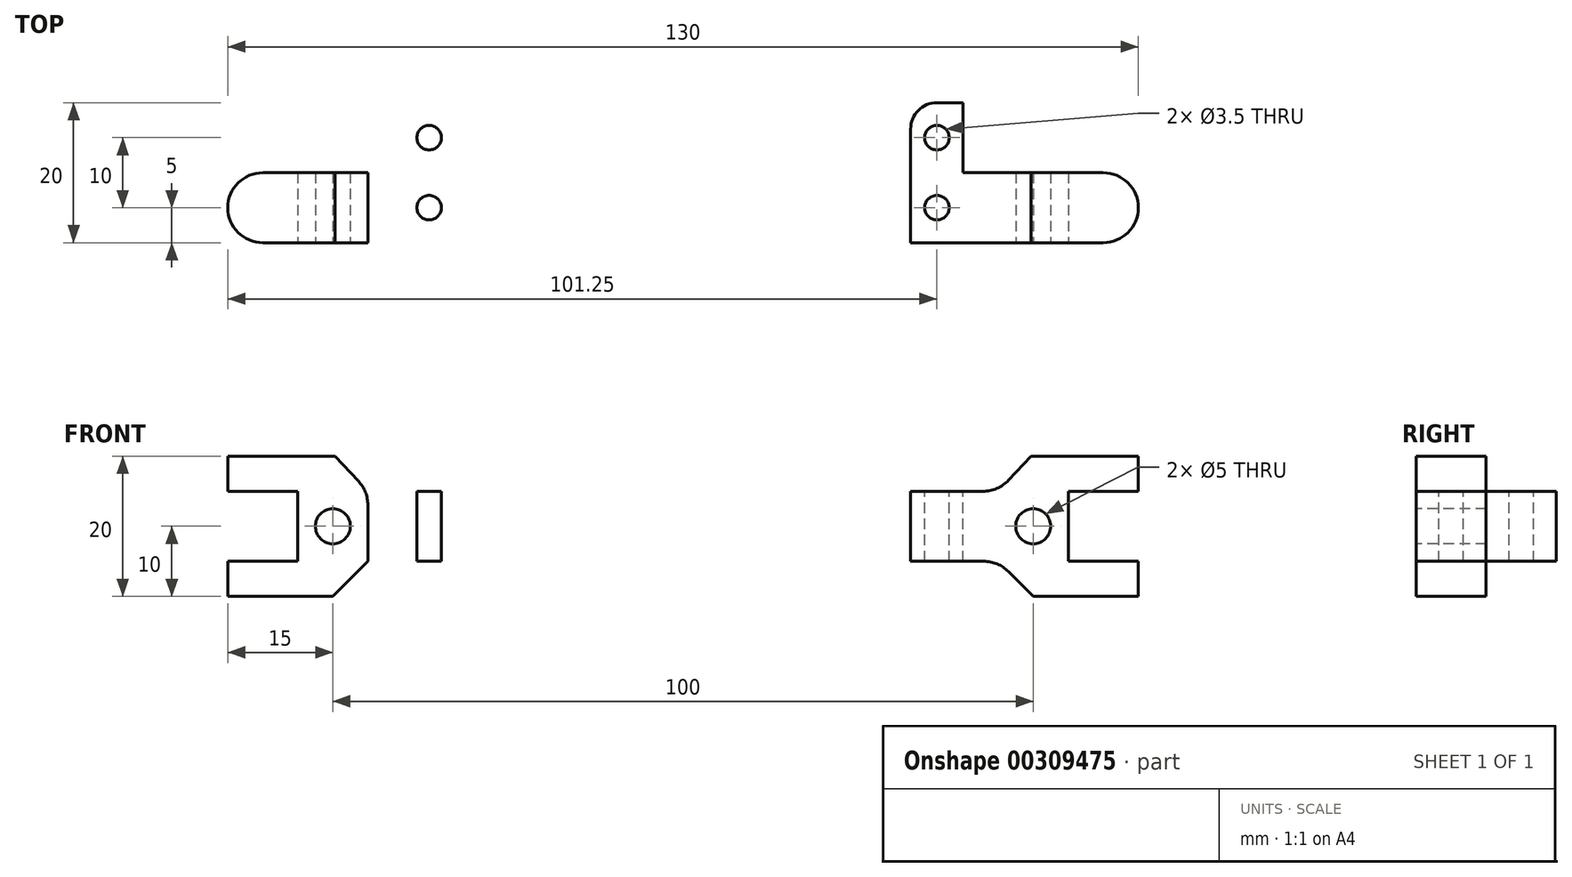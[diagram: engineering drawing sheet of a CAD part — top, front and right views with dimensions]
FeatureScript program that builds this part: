
annotation { "Feature Type Name" : "Feature", "Feature Type Description" : "" }
export const myFeature = defineFeature(function(context is Context, id is Id, definition is map)
    precondition{}
    {
        {
            var Q0;
            Q0=qCreatedBy(makeId("Top.planeOp"),FACE);
            var sketch = newSketch(context, id + "F0", { "sketchPlane" : qUnion([Q0])});
            skLineSegment(sketch, "E0.bottom", {"start": v(65, 5) * mm, "end": v(-65, 5) * mm});
            skLineSegment(sketch, "E0.top", {"start": v(65, -5) * mm, "end": v(-65, -5) * mm});
            skLineSegment(sketch, "E0.left", {"start": v(65, 5) * mm, "end": v(65, -5) * mm});
            skLineSegment(sketch, "E0.right", {"start": v(-65, 5) * mm, "end": v(-65, -5) * mm});
            skPoint(sketch, "E0.middle", {"position": v(0, 0) * mm});
            skSolve(sketch);
        }
        {
            var Q0;
            Q0 = qSketchRegion(id + "F0", true);
            extrude(context, id + "F1", {"entities" : qUnion([Q0]), "depth" : 20 * mm, "offsetDistance" : 25 * mm});
        }
        {
            var Q0;
            Q0=makeQuery(id+"F1.opExtrude","SWEPT_FACE",FACE,{"disambiguationData":[OSD([sQuery(id+"F0.wireOp",EDGE,"E0.top")])]});
            var sketch = newSketch(context, id + "F2", { "sketchPlane" : qUnion([Q0])});
            skLineSegment(sketch, "E1", {"start": v(0, 0) * mm, "end": v(0, 10) * mm});
            skLineSegment(sketch, "E2.bottom", {"start": v(-55, 15) * mm, "end": v(55, 15) * mm});
            skLineSegment(sketch, "E2.top", {"start": v(-55, 5) * mm, "end": v(55, 5) * mm});
            skLineSegment(sketch, "E2.left", {"start": v(-55, 15) * mm, "end": v(-55, 5) * mm});
            skLineSegment(sketch, "E2.right", {"start": v(55, 15) * mm, "end": v(55, 5) * mm});
            skPoint(sketch, "E2.middle", {"position": v(0, 10) * mm});
            skLineSegment(sketch, "E3", {"start": v(-55, 15) * mm, "end": v(-65, 15) * mm});
            skLineSegment(sketch, "E4", {"start": v(-55, 5) * mm, "end": v(-65, 5) * mm});
            skLineSegment(sketch, "E5", {"start": v(55, 15) * mm, "end": v(65, 15) * mm});
            skPoint(sketch, "E5.endSnap0", {"position": v(65, 10) * mm});
            skLineSegment(sketch, "E6", {"start": v(55, 5) * mm, "end": v(65, 5) * mm});
            skLineSegment(sketch, "E7", {"start": v(-55, 5) * mm, "end": v(-55, 0) * mm});
            skLineSegment(sketch, "E8", {"start": v(-55, 0) * mm, "end": v(-50, 0) * mm});
            skLineSegment(sketch, "E9", {"start": v(-50, 0) * mm, "end": v(-45, 5) * mm});
            skLineSegment(sketch, "E10", {"start": v(-54.7, 20) * mm, "end": v(-49.7, 20) * mm});
            skLineSegment(sketch, "E11", {"start": v(-45, 5) * mm, "end": v(-45, 15) * mm});
            skLineSegment(sketch, "E12", {"start": v(-45, 15) * mm, "end": v(-49.7, 20) * mm});
            skLineSegment(sketch, "E13", {"start": v(-45, 15) * mm, "end": v(-55, 5) * mm});
            skLineSegment(sketch, "E14", {"start": v(-55, 15) * mm, "end": v(-45, 5) * mm});
            skCircle(sketch, "E15", {"center": v(-50, 10) * mm, "radius": 2.5 * mm});
            skCircle(sketch, "E16", {"center": v(0, 10) * mm, "radius": 2 * mm});
            skLineSegment(sketch, "E17", {"start": v(-50, 10) * mm, "end": v(55, 10) * mm});
            skCircle(sketch, "E18.MirrorC", {"center": v(50, 10) * mm, "radius": 2.5 * mm});
            skLineSegment(sketch, "E19.MirrorCS", {"start": v(45, 15) * mm, "end": v(49.7, 20) * mm});
            skLineSegment(sketch, "E20.MirrorCS", {"start": v(50, 0) * mm, "end": v(45, 5) * mm});
            skLineSegment(sketch, "E21", {"start": v(0, 10) * mm, "end": v(-15, 10) * mm});
            skLineSegment(sketch, "E22", {"start": v(-15, 10) * mm, "end": v(-30, 10) * mm});
            skCircle(sketch, "E23", {"center": v(-15, 10) * mm, "radius": 2 * mm});
            skCircle(sketch, "E24", {"center": v(-30, 10) * mm, "radius": 2 * mm});
            skCircle(sketch, "E25.MirrorC", {"center": v(15, 10) * mm, "radius": 2 * mm});
            skCircle(sketch, "E26.MirrorC", {"center": v(30, 10) * mm, "radius": 2 * mm});
            skSolve(sketch);
        }
        {
            var Q0;
            Q0=makeQuery(id+"F2.imprint","IMPRINT",FACE,{"disambiguationData":[TD([[makeQuery(id+"F2.imprint","IMPRINT",EDGE,{"derivedFrom":sQuery(id+"F2.wireOp",EDGE,"E2.left")}),-1.0]])]});
            var Q1;
            {var subQ5=sQuery(id+"F2.wireOp",EDGE,"E9");Q1=makeQuery(id+"F2.imprint","IMPRINT",FACE,{"disambiguationData":[TD([[makeQuery(id+"F2.imprint","IMPRINT",EDGE,{"derivedFrom":subQ5}),-1.0]])]});}
            var Q2;
            {var subQ0=sQuery(id+"F2.wireOp",EDGE,"E12");Q2=makeQuery(id+"F2.imprint","IMPRINT",FACE,{"disambiguationData":[TD([[makeQuery(id+"F2.imprint","IMPRINT",EDGE,{"derivedFrom":subQ0}),-1.0]])]});}
            var Q3;
            {var subQ5=sQuery(id+"F2.wireOp",EDGE,"E20.MirrorCS");Q3=makeQuery(id+"F2.imprint","IMPRINT",FACE,{"disambiguationData":[TD([[makeQuery(id+"F2.imprint","IMPRINT",EDGE,{"derivedFrom":subQ5}),1.0]])]});}
            var Q4;
            {var subQ0=sQuery(id+"F2.wireOp",EDGE,"E5");Q4=makeQuery(id+"F2.imprint","IMPRINT",FACE,{"disambiguationData":[TD([[makeQuery(id+"F2.imprint","IMPRINT",EDGE,{"derivedFrom":subQ0}),-1.0]])]});}
            var Q5;
            {var subQ0=sQuery(id+"F2.wireOp",EDGE,"E18.MirrorC");var subQ1=sQuery(id+"F2.wireOp",EDGE,"E17");var subQ2=makeQuery(id+"F2.imprint","INTERSECT",VERTEX,{"disambiguationData":[OD(0.0)],"derivedFrom":[subQ1,subQ0]});Q5=makeQuery(id+"F2.imprint","IMPRINT",FACE,{"disambiguationData":[TD([[makeQuery(id+"F2.imprint","IMPRINT",EDGE,{"disambiguationData":[TD([[subQ2,-1.0]])],"derivedFrom":subQ1}),1.0]])]});}
            var Q6;
            {var subQ0=sQuery(id+"F2.wireOp",EDGE,"E18.MirrorC");var subQ1=sQuery(id+"F2.wireOp",EDGE,"E17");var subQ2=makeQuery(id+"F2.imprint","INTERSECT",VERTEX,{"disambiguationData":[OD(0.0)],"derivedFrom":[subQ1,subQ0]});Q6=makeQuery(id+"F2.imprint","IMPRINT",FACE,{"disambiguationData":[TD([[makeQuery(id+"F2.imprint","IMPRINT",EDGE,{"disambiguationData":[TD([[subQ2,-1.0]])],"derivedFrom":subQ1}),-1.0]])]});}
            var Q7;
            {var subQ0=sQuery(id+"F2.wireOp",EDGE,"E26.MirrorC");var subQ1=sQuery(id+"F2.wireOp",EDGE,"E17");var subQ2=makeQuery(id+"F2.imprint","INTERSECT",VERTEX,{"disambiguationData":[OD(0.0)],"derivedFrom":[subQ1,subQ0]});Q7=makeQuery(id+"F2.imprint","IMPRINT",FACE,{"disambiguationData":[TD([[makeQuery(id+"F2.imprint","IMPRINT",EDGE,{"disambiguationData":[TD([[subQ2,-1.0]])],"derivedFrom":subQ1}),1.0]])]});}
            var Q8;
            {var subQ0=sQuery(id+"F2.wireOp",EDGE,"E26.MirrorC");var subQ1=sQuery(id+"F2.wireOp",EDGE,"E17");var subQ2=makeQuery(id+"F2.imprint","INTERSECT",VERTEX,{"disambiguationData":[OD(0.0)],"derivedFrom":[subQ1,subQ0]});Q8=makeQuery(id+"F2.imprint","IMPRINT",FACE,{"disambiguationData":[TD([[makeQuery(id+"F2.imprint","IMPRINT",EDGE,{"disambiguationData":[TD([[subQ2,-1.0]])],"derivedFrom":subQ1}),-1.0]])]});}
            var Q9;
            {var subQ0=sQuery(id+"F2.wireOp",EDGE,"E25.MirrorC");var subQ1=sQuery(id+"F2.wireOp",EDGE,"E17");var subQ2=makeQuery(id+"F2.imprint","INTERSECT",VERTEX,{"disambiguationData":[OD(0.0)],"derivedFrom":[subQ1,subQ0]});Q9=makeQuery(id+"F2.imprint","IMPRINT",FACE,{"disambiguationData":[TD([[makeQuery(id+"F2.imprint","IMPRINT",EDGE,{"disambiguationData":[TD([[subQ2,-1.0]])],"derivedFrom":subQ1}),1.0]])]});}
            var Q10;
            {var subQ0=sQuery(id+"F2.wireOp",EDGE,"E25.MirrorC");var subQ1=sQuery(id+"F2.wireOp",EDGE,"E17");var subQ2=makeQuery(id+"F2.imprint","INTERSECT",VERTEX,{"disambiguationData":[OD(0.0)],"derivedFrom":[subQ1,subQ0]});Q10=makeQuery(id+"F2.imprint","IMPRINT",FACE,{"disambiguationData":[TD([[makeQuery(id+"F2.imprint","IMPRINT",EDGE,{"disambiguationData":[TD([[subQ2,-1.0]])],"derivedFrom":subQ1}),-1.0]])]});}
            var Q11;
            {var subQ0=sQuery(id+"F2.wireOp",EDGE,"E21");var subQ1=sQuery(id+"F2.wireOp",EDGE,"E16");var subQ2=makeQuery(id+"F2.imprint","INTERSECT",VERTEX,{"derivedFrom":[subQ1,subQ0]});Q11=makeQuery(id+"F2.imprint","IMPRINT",FACE,{"disambiguationData":[TD([[makeQuery(id+"F2.imprint","IMPRINT",EDGE,{"disambiguationData":[TD([[subQ2,1.0]])],"derivedFrom":subQ1}),1.0]])]});}
            var Q12;
            {var subQ1=sQuery(id+"F2.wireOp",EDGE,"E1");var subQ3=sQuery(id+"F2.wireOp",EDGE,"E16");var subQ4=makeQuery(id+"F2.imprint","INTERSECT",VERTEX,{"derivedFrom":[subQ1,subQ3]});Q12=makeQuery(id+"F2.imprint","IMPRINT",FACE,{"disambiguationData":[TD([[makeQuery(id+"F2.imprint","IMPRINT",EDGE,{"disambiguationData":[TD([[subQ4,-1.0]])],"derivedFrom":subQ3}),1.0]])]});}
            var Q13;
            {var subQ1=sQuery(id+"F2.wireOp",EDGE,"E1");var subQ3=sQuery(id+"F2.wireOp",EDGE,"E16");var subQ4=makeQuery(id+"F2.imprint","INTERSECT",VERTEX,{"derivedFrom":[subQ1,subQ3]});Q13=makeQuery(id+"F2.imprint","IMPRINT",FACE,{"disambiguationData":[TD([[makeQuery(id+"F2.imprint","IMPRINT",EDGE,{"disambiguationData":[TD([[subQ4,1.0]])],"derivedFrom":subQ3}),1.0]])]});}
            var Q14;
            {var subQ0=sQuery(id+"F2.wireOp",EDGE,"E22");var subQ1=sQuery(id+"F2.wireOp",EDGE,"E21");var subQ2=makeQuery(id+"F2.imprint","INTERSECT",VERTEX,{"derivedFrom":[subQ1,subQ0]});Q14=makeQuery(id+"F2.imprint","IMPRINT",FACE,{"disambiguationData":[TD([[makeQuery(id+"F2.imprint","IMPRINT",EDGE,{"disambiguationData":[TD([[subQ2,1.0]])],"derivedFrom":subQ1}),-1.0]])]});}
            var Q15;
            {var subQ0=sQuery(id+"F2.wireOp",EDGE,"E22");var subQ1=sQuery(id+"F2.wireOp",EDGE,"E21");var subQ2=makeQuery(id+"F2.imprint","INTERSECT",VERTEX,{"derivedFrom":[subQ1,subQ0]});Q15=makeQuery(id+"F2.imprint","IMPRINT",FACE,{"disambiguationData":[TD([[makeQuery(id+"F2.imprint","IMPRINT",EDGE,{"disambiguationData":[TD([[subQ2,1.0]])],"derivedFrom":subQ1}),1.0]])]});}
            var Q16;
            {var subQ0=sQuery(id+"F2.wireOp",EDGE,"E22");var subQ1=sQuery(id+"F2.wireOp",EDGE,"E17");var subQ2=makeQuery(id+"F2.imprint","INTERSECT",VERTEX,{"derivedFrom":[subQ1,subQ0]});Q16=makeQuery(id+"F2.imprint","IMPRINT",FACE,{"disambiguationData":[TD([[makeQuery(id+"F2.imprint","IMPRINT",EDGE,{"disambiguationData":[TD([[subQ2,1.0]])],"derivedFrom":subQ1}),1.0]])]});}
            var Q17;
            {var subQ0=sQuery(id+"F2.wireOp",EDGE,"E22");var subQ1=sQuery(id+"F2.wireOp",EDGE,"E17");var subQ2=makeQuery(id+"F2.imprint","INTERSECT",VERTEX,{"derivedFrom":[subQ1,subQ0]});Q17=makeQuery(id+"F2.imprint","IMPRINT",FACE,{"disambiguationData":[TD([[makeQuery(id+"F2.imprint","IMPRINT",EDGE,{"disambiguationData":[TD([[subQ2,1.0]])],"derivedFrom":subQ1}),-1.0]])]});}
            var Q18;
            {var subQ1=sQuery(id+"F2.wireOp",EDGE,"E13");var subQ3=sQuery(id+"F2.wireOp",EDGE,"E15");var subQ4=makeQuery(id+"F2.imprint","INTERSECT",VERTEX,{"disambiguationData":[OD(0.0)],"derivedFrom":[subQ1,subQ3]});Q18=makeQuery(id+"F2.imprint","IMPRINT",FACE,{"disambiguationData":[TD([[makeQuery(id+"F2.imprint","IMPRINT",EDGE,{"disambiguationData":[TD([[subQ4,1.0]])],"derivedFrom":subQ3}),1.0]])]});}
            var Q19;
            {var subQ1=sQuery(id+"F2.wireOp",EDGE,"E13");var subQ3=sQuery(id+"F2.wireOp",EDGE,"E15");var subQ4=makeQuery(id+"F2.imprint","INTERSECT",VERTEX,{"disambiguationData":[OD(0.0)],"derivedFrom":[subQ1,subQ3]});Q19=makeQuery(id+"F2.imprint","IMPRINT",FACE,{"disambiguationData":[TD([[makeQuery(id+"F2.imprint","IMPRINT",EDGE,{"disambiguationData":[TD([[subQ4,-1.0]])],"derivedFrom":subQ3}),1.0]])]});}
            var Q20;
            {var subQ1=sQuery(id+"F2.wireOp",EDGE,"E13");var subQ3=sQuery(id+"F2.wireOp",EDGE,"E15");var subQ4=makeQuery(id+"F2.imprint","INTERSECT",VERTEX,{"disambiguationData":[OD(1.0)],"derivedFrom":[subQ1,subQ3]});Q20=makeQuery(id+"F2.imprint","IMPRINT",FACE,{"disambiguationData":[TD([[makeQuery(id+"F2.imprint","IMPRINT",EDGE,{"disambiguationData":[TD([[subQ4,1.0]])],"derivedFrom":subQ3}),1.0]])]});}
            var Q21;
            {var subQ1=sQuery(id+"F2.wireOp",EDGE,"E13");var subQ3=sQuery(id+"F2.wireOp",EDGE,"E15");var subQ4=makeQuery(id+"F2.imprint","INTERSECT",VERTEX,{"disambiguationData":[OD(1.0)],"derivedFrom":[subQ1,subQ3]});Q21=makeQuery(id+"F2.imprint","IMPRINT",FACE,{"disambiguationData":[TD([[makeQuery(id+"F2.imprint","IMPRINT",EDGE,{"disambiguationData":[TD([[subQ4,-1.0]])],"derivedFrom":subQ3}),1.0]])]});}
            var Q22;
            {var subQ1=sQuery(id+"F2.wireOp",EDGE,"E14");var subQ3=sQuery(id+"F2.wireOp",EDGE,"E15");var subQ4=makeQuery(id+"F2.imprint","INTERSECT",VERTEX,{"disambiguationData":[OD(1.0)],"derivedFrom":[subQ1,subQ3]});Q22=makeQuery(id+"F2.imprint","IMPRINT",FACE,{"disambiguationData":[TD([[makeQuery(id+"F2.imprint","IMPRINT",EDGE,{"disambiguationData":[TD([[subQ4,-1.0]])],"derivedFrom":subQ3}),1.0]])]});}
            extrude(context, id + "F3", {"entities" : qUnion([Q0, Q1, Q2, Q3, Q4, Q5, Q6, Q7, Q8, Q9, Q10, Q11, Q12, Q13, Q14, Q15, Q16, Q17, Q18, Q19, Q20, Q21, Q22]), "operationType" : NewBodyOperationType.REMOVE, "oppositeDirection" : true, "depth" : 25 * mm, "offsetDistance" : 25 * mm});
        }
        {
            var Q0;
            Q0=makeQuery(id+"F1.opExtrude","SWEPT_FACE",FACE,{"disambiguationData":[OSD([sQuery(id+"F0.wireOp",EDGE,"E0.bottom")])]});
            var sketch = newSketch(context, id + "F4", { "sketchPlane" : qUnion([Q0])});
            skLineSegment(sketch, "E27.bottom", {"start": v(-45, 5) * mm, "end": v(-40, 5) * mm});
            skLineSegment(sketch, "E27.top", {"start": v(-45, 15) * mm, "end": v(-40, 15) * mm});
            skLineSegment(sketch, "E27.left", {"start": v(-45, 5) * mm, "end": v(-45, 15) * mm});
            skLineSegment(sketch, "E27.right", {"start": v(-40, 5) * mm, "end": v(-40, 15) * mm});
            skLineSegment(sketch, "E28.bottom", {"start": v(-40, 15) * mm, "end": v(-32.5, 15) * mm});
            skLineSegment(sketch, "E28.top", {"start": v(-40, 5) * mm, "end": v(-32.5, 5) * mm});
            skLineSegment(sketch, "E28.left", {"start": v(-40, 15) * mm, "end": v(-40, 5) * mm});
            skLineSegment(sketch, "E28.right", {"start": v(-32.5, 15) * mm, "end": v(-32.5, 5) * mm});
            skLineSegment(sketch, "E29.MirrorCS", {"start": v(40, 15) * mm, "end": v(40, 5) * mm});
            skLineSegment(sketch, "E30.MirrorCS", {"start": v(32.5, 15) * mm, "end": v(32.5, 5) * mm});
            skSolve(sketch);
        }
        {
            var Q0;
            Q0=makeQuery(id+"F4.imprint","IMPRINT",FACE,{"disambiguationData":[TD([[makeQuery(id+"F4.imprint","IMPRINT",EDGE,{"derivedFrom":sQuery(id+"F4.wireOp",EDGE,"E28.bottom")}),1.0]])]});
            var Q1;
            {var subQ0=sQuery(id+"F4.wireOp",EDGE,"E29.MirrorCS");Q1=makeQuery(id+"F4.imprint","IMPRINT",FACE,{"disambiguationData":[TD([[makeQuery(id+"F4.imprint","IMPRINT",EDGE,{"derivedFrom":subQ0}),-1.0]])]});}
            extrude(context, id + "F5", {"entities" : qUnion([Q0, Q1]), "operationType" : NewBodyOperationType.ADD, "depth" : 10 * mm, "offsetDistance" : 25 * mm});
        }
        {
            var Q0;
            {var subQ0=sQuery(id+"F2.wireOp",EDGE,"E2.bottom");Q0=makeQuery(id+"F5.boolean.opBoolean","MERGE",FACE,{"derivedFrom":[makeQuery(id+"F3.boolean.opBoolean","COPY",FACE,{"derivedFrom":makeQuery(id+"F3.opExtrude","SWEPT_FACE",FACE,{"disambiguationData":[OSD([subQ0])]})}),makeQuery(id+"F5.opExtrude","SWEPT_FACE",FACE,{"disambiguationData":[OSD([sQuery(id+"F4.wireOp",EDGE,"E28.bottom")])]}),makeQuery(id+"F5.opExtrude","SWEPT_FACE",FACE,{"disambiguationData":[OSD([sQuery(id+"F0.wireOp",EDGE,"E0.bottom"),subQ0])]})]});}
            var sketch = newSketch(context, id + "F6", { "sketchPlane" : qUnion([Q0])});
            skLineSegment(sketch, "E31.bottom", {"start": v(32.5, 15) * mm, "end": v(40, 15) * mm});
            skLineSegment(sketch, "E31.top", {"start": v(32.5, -5) * mm, "end": v(40, -5) * mm});
            skLineSegment(sketch, "E31.left", {"start": v(32.5, 15) * mm, "end": v(32.5, -5) * mm});
            skLineSegment(sketch, "E31.right", {"start": v(40, 15) * mm, "end": v(40, -5) * mm});
            skLineSegment(sketch, "E32", {"start": v(40, -5) * mm, "end": v(32.5, 5) * mm});
            skLineSegment(sketch, "E33", {"start": v(32.5, 5) * mm, "end": v(40, 15) * mm});
            skLineSegment(sketch, "E34", {"start": v(32.5, 15) * mm, "end": v(40, 5) * mm});
            skLineSegment(sketch, "E35", {"start": v(40, 5) * mm, "end": v(32.5, -5) * mm});
            skCircle(sketch, "E36", {"center": v(36.25, 0) * mm, "radius": 1.75 * mm});
            skCircle(sketch, "E37", {"center": v(36.25, 10) * mm, "radius": 1.75 * mm});
            skCircle(sketch, "E38.MirrorC", {"center": v(-36.25, 0) * mm, "radius": 1.75 * mm});
            skCircle(sketch, "E39.MirrorC", {"center": v(-36.25, 10) * mm, "radius": 1.75 * mm});
            skSolve(sketch);
        }
        {
            var Q0;
            {var subQ0=sQuery(id+"F6.wireOp",EDGE,"E35");var subQ1=sQuery(id+"F6.wireOp",EDGE,"E32");var subQ2=makeQuery(id+"F6.imprint","INTERSECT",VERTEX,{"derivedFrom":[subQ1,subQ0]});Q0=makeQuery(id+"F6.imprint","IMPRINT",FACE,{"disambiguationData":[TD([[makeQuery(id+"F6.imprint","IMPRINT",EDGE,{"disambiguationData":[TD([[subQ2,-1.0]])],"derivedFrom":subQ1}),1.0]])]});}
            var Q1;
            {var subQ0=sQuery(id+"F6.wireOp",EDGE,"E36");var subQ1=sQuery(id+"F6.wireOp",EDGE,"E32");var subQ2=makeQuery(id+"F6.imprint","INTERSECT",VERTEX,{"disambiguationData":[OD(0.0)],"derivedFrom":[subQ1,subQ0]});Q1=makeQuery(id+"F6.imprint","IMPRINT",FACE,{"disambiguationData":[TD([[makeQuery(id+"F6.imprint","IMPRINT",EDGE,{"disambiguationData":[TD([[subQ2,-1.0]])],"derivedFrom":subQ1}),1.0]])]});}
            var Q2;
            {var subQ0=sQuery(id+"F6.wireOp",EDGE,"E36");var subQ1=sQuery(id+"F6.wireOp",EDGE,"E32");var subQ2=makeQuery(id+"F6.imprint","INTERSECT",VERTEX,{"disambiguationData":[OD(0.0)],"derivedFrom":[subQ1,subQ0]});Q2=makeQuery(id+"F6.imprint","IMPRINT",FACE,{"disambiguationData":[TD([[makeQuery(id+"F6.imprint","IMPRINT",EDGE,{"disambiguationData":[TD([[subQ2,-1.0]])],"derivedFrom":subQ1}),-1.0]])]});}
            var Q3;
            {var subQ0=sQuery(id+"F6.wireOp",EDGE,"E35");var subQ1=sQuery(id+"F6.wireOp",EDGE,"E32");var subQ2=makeQuery(id+"F6.imprint","INTERSECT",VERTEX,{"derivedFrom":[subQ1,subQ0]});Q3=makeQuery(id+"F6.imprint","IMPRINT",FACE,{"disambiguationData":[TD([[makeQuery(id+"F6.imprint","IMPRINT",EDGE,{"disambiguationData":[TD([[subQ2,-1.0]])],"derivedFrom":subQ1}),-1.0]])]});}
            var Q4;
            {var subQ0=sQuery(id+"F6.wireOp",EDGE,"E37");var subQ1=sQuery(id+"F6.wireOp",EDGE,"E33");var subQ2=makeQuery(id+"F6.imprint","INTERSECT",VERTEX,{"disambiguationData":[OD(0.0)],"derivedFrom":[subQ1,subQ0]});Q4=makeQuery(id+"F6.imprint","IMPRINT",FACE,{"disambiguationData":[TD([[makeQuery(id+"F6.imprint","IMPRINT",EDGE,{"disambiguationData":[TD([[subQ2,-1.0]])],"derivedFrom":subQ1}),1.0]])]});}
            var Q5;
            {var subQ0=sQuery(id+"F6.wireOp",EDGE,"E37");var subQ1=sQuery(id+"F6.wireOp",EDGE,"E33");var subQ2=makeQuery(id+"F6.imprint","INTERSECT",VERTEX,{"disambiguationData":[OD(0.0)],"derivedFrom":[subQ1,subQ0]});Q5=makeQuery(id+"F6.imprint","IMPRINT",FACE,{"disambiguationData":[TD([[makeQuery(id+"F6.imprint","IMPRINT",EDGE,{"disambiguationData":[TD([[subQ2,-1.0]])],"derivedFrom":subQ1}),-1.0]])]});}
            var Q6;
            {var subQ0=sQuery(id+"F6.wireOp",EDGE,"E34");var subQ1=sQuery(id+"F6.wireOp",EDGE,"E33");var subQ2=makeQuery(id+"F6.imprint","INTERSECT",VERTEX,{"derivedFrom":[subQ1,subQ0]});Q6=makeQuery(id+"F6.imprint","IMPRINT",FACE,{"disambiguationData":[TD([[makeQuery(id+"F6.imprint","IMPRINT",EDGE,{"disambiguationData":[TD([[subQ2,-1.0]])],"derivedFrom":subQ1}),-1.0]])]});}
            var Q7;
            {var subQ0=sQuery(id+"F6.wireOp",EDGE,"E34");var subQ1=sQuery(id+"F6.wireOp",EDGE,"E33");var subQ2=makeQuery(id+"F6.imprint","INTERSECT",VERTEX,{"derivedFrom":[subQ1,subQ0]});Q7=makeQuery(id+"F6.imprint","IMPRINT",FACE,{"disambiguationData":[TD([[makeQuery(id+"F6.imprint","IMPRINT",EDGE,{"disambiguationData":[TD([[subQ2,-1.0]])],"derivedFrom":subQ1}),1.0]])]});}
            var Q8;
            Q8=makeQuery(id+"F6.imprint","IMPRINT",FACE,{"disambiguationData":[TD([[makeQuery(id+"F6.imprint","IMPRINT",EDGE,{"derivedFrom":sQuery(id+"F6.wireOp",EDGE,"E38.MirrorC")}),-1.0]])]});
            var Q9;
            Q9=makeQuery(id+"F6.imprint","IMPRINT",FACE,{"disambiguationData":[TD([[makeQuery(id+"F6.imprint","IMPRINT",EDGE,{"derivedFrom":sQuery(id+"F6.wireOp",EDGE,"E39.MirrorC")}),-1.0]])]});
            extrude(context, id + "F7", {"entities" : qUnion([Q0, Q1, Q2, Q3, Q4, Q5, Q6, Q7, Q8, Q9]), "operationType" : NewBodyOperationType.REMOVE, "oppositeDirection" : true, "depth" : 25 * mm, "offsetDistance" : 25 * mm});
        }
        {
            var Q0;
            {var subQ0=sQuery(id+"F0.wireOp",EDGE,"E0.bottom");var subQ1=sQuery(id+"F0.wireOp",EDGE,"E0.right");Q0=makeQuery(id+"F3.boolean.opBoolean","SPLIT",EDGE,{"disambiguationData":[TD([makeQuery(id+"F3.opExtrude","SWEPT_FACE",FACE,{"disambiguationData":[OSD([sQuery(id+"F2.wireOp",EDGE,"E4")])]})])],"derivedFrom":makeQuery(id+"F1.opExtrude","SWEPT_EDGE",EDGE,{"disambiguationData":[OSD([subQ0,subQ1])]})});}
            var Q1;
            {var subQ0=sQuery(id+"F0.wireOp",EDGE,"E0.bottom");var subQ1=sQuery(id+"F0.wireOp",EDGE,"E0.right");Q1=makeQuery(id+"F3.boolean.opBoolean","SPLIT",EDGE,{"disambiguationData":[TD([makeQuery(id+"F3.opExtrude","SWEPT_FACE",FACE,{"disambiguationData":[OSD([sQuery(id+"F2.wireOp",EDGE,"E3")])]})])],"derivedFrom":makeQuery(id+"F1.opExtrude","SWEPT_EDGE",EDGE,{"disambiguationData":[OSD([subQ0,subQ1])]})});}
            var Q2;
            {var subQ0=sQuery(id+"F0.wireOp",EDGE,"E0.right");var subQ1=sQuery(id+"F0.wireOp",EDGE,"E0.top");Q2=makeQuery(id+"F3.boolean.opBoolean","SPLIT",EDGE,{"disambiguationData":[TD([makeQuery(id+"F3.opExtrude","SWEPT_FACE",FACE,{"disambiguationData":[OSD([sQuery(id+"F2.wireOp",EDGE,"E4")])]})])],"derivedFrom":makeQuery(id+"F1.opExtrude","SWEPT_EDGE",EDGE,{"disambiguationData":[OSD([subQ1,subQ0])]})});}
            var Q3;
            {var subQ0=sQuery(id+"F0.wireOp",EDGE,"E0.right");var subQ1=sQuery(id+"F0.wireOp",EDGE,"E0.top");Q3=makeQuery(id+"F3.boolean.opBoolean","SPLIT",EDGE,{"disambiguationData":[TD([makeQuery(id+"F3.opExtrude","SWEPT_FACE",FACE,{"disambiguationData":[OSD([sQuery(id+"F2.wireOp",EDGE,"E3")])]})])],"derivedFrom":makeQuery(id+"F1.opExtrude","SWEPT_EDGE",EDGE,{"disambiguationData":[OSD([subQ1,subQ0])]})});}
            var Q4;
            {var subQ0=sQuery(id+"F0.wireOp",EDGE,"E0.bottom");var subQ1=sQuery(id+"F0.wireOp",EDGE,"E0.left");Q4=makeQuery(id+"F3.boolean.opBoolean","SPLIT",EDGE,{"disambiguationData":[TD([makeQuery(id+"F3.opExtrude","SWEPT_FACE",FACE,{"disambiguationData":[OSD([sQuery(id+"F2.wireOp",EDGE,"E5")])]})])],"derivedFrom":makeQuery(id+"F1.opExtrude","SWEPT_EDGE",EDGE,{"disambiguationData":[OSD([subQ0,subQ1])]})});}
            var Q5;
            {var subQ0=sQuery(id+"F0.wireOp",EDGE,"E0.bottom");var subQ1=sQuery(id+"F0.wireOp",EDGE,"E0.left");Q5=makeQuery(id+"F3.boolean.opBoolean","SPLIT",EDGE,{"disambiguationData":[TD([makeQuery(id+"F3.opExtrude","SWEPT_FACE",FACE,{"disambiguationData":[OSD([sQuery(id+"F2.wireOp",EDGE,"E6")])]})])],"derivedFrom":makeQuery(id+"F1.opExtrude","SWEPT_EDGE",EDGE,{"disambiguationData":[OSD([subQ0,subQ1])]})});}
            var Q6;
            {var subQ0=sQuery(id+"F0.wireOp",EDGE,"E0.left");var subQ1=sQuery(id+"F0.wireOp",EDGE,"E0.top");Q6=makeQuery(id+"F3.boolean.opBoolean","SPLIT",EDGE,{"disambiguationData":[TD([makeQuery(id+"F3.opExtrude","SWEPT_FACE",FACE,{"disambiguationData":[OSD([sQuery(id+"F2.wireOp",EDGE,"E5")])]})])],"derivedFrom":makeQuery(id+"F1.opExtrude","SWEPT_EDGE",EDGE,{"disambiguationData":[OSD([subQ1,subQ0])]})});}
            var Q7;
            {var subQ0=sQuery(id+"F0.wireOp",EDGE,"E0.left");var subQ1=sQuery(id+"F0.wireOp",EDGE,"E0.top");Q7=makeQuery(id+"F3.boolean.opBoolean","SPLIT",EDGE,{"disambiguationData":[TD([makeQuery(id+"F3.opExtrude","SWEPT_FACE",FACE,{"disambiguationData":[OSD([sQuery(id+"F2.wireOp",EDGE,"E6")])]})])],"derivedFrom":makeQuery(id+"F1.opExtrude","SWEPT_EDGE",EDGE,{"disambiguationData":[OSD([subQ1,subQ0])]})});}
            var Q8;
            Q8=makeQuery(id+"F3.boolean.opBoolean","COPY",EDGE,{"derivedFrom":makeQuery(id+"F3.opExtrude","SWEPT_EDGE",EDGE,{"disambiguationData":[OSD([sQuery(id+"F0.wireOp",EDGE,"E0.top"),sQuery(id+"F2.wireOp",EDGE,"E20.MirrorCS")])]})});
            var Q9;
            Q9=makeQuery(id+"F3.boolean.opBoolean","COPY",EDGE,{"derivedFrom":makeQuery(id+"F3.opExtrude","SWEPT_EDGE",EDGE,{"disambiguationData":[OSD([sQuery(id+"F0.wireOp",EDGE,"E0.top"),sQuery(id+"F2.wireOp",EDGE,"E19.MirrorCS")])]})});
            var Q10;
            Q10=makeQuery(id+"F3.boolean.opBoolean","COPY",EDGE,{"derivedFrom":makeQuery(id+"F3.opExtrude","SWEPT_EDGE",EDGE,{"disambiguationData":[OSD([sQuery(id+"F0.wireOp",EDGE,"E0.top"),sQuery(id+"F2.wireOp",EDGE,"E10"),sQuery(id+"F2.wireOp",EDGE,"E12")])]})});
            var Q11;
            Q11=makeQuery(id+"F3.boolean.opBoolean","COPY",EDGE,{"derivedFrom":makeQuery(id+"F3.opExtrude","SWEPT_EDGE",EDGE,{"disambiguationData":[OSD([sQuery(id+"F0.wireOp",EDGE,"E0.top"),sQuery(id+"F2.wireOp",EDGE,"E8"),sQuery(id+"F2.wireOp",EDGE,"E9")])]})});
            var Q12;
            Q12=makeQuery(id+"F3.boolean.opBoolean","COPY",EDGE,{"derivedFrom":makeQuery(id+"F3.opExtrude","SWEPT_EDGE",EDGE,{"disambiguationData":[OSD([sQuery(id+"F2.wireOp",EDGE,"E2.top"),sQuery(id+"F2.wireOp",EDGE,"E9"),sQuery(id+"F2.wireOp",EDGE,"E11"),sQuery(id+"F2.wireOp",EDGE,"E14")])]})});
            var Q13;
            Q13=makeQuery(id+"F3.boolean.opBoolean","COPY",EDGE,{"derivedFrom":makeQuery(id+"F3.opExtrude","SWEPT_EDGE",EDGE,{"disambiguationData":[OSD([sQuery(id+"F2.wireOp",EDGE,"E2.top"),sQuery(id+"F2.wireOp",EDGE,"E20.MirrorCS")])]})});
            var Q14;
            Q14=makeQuery(id+"F3.boolean.opBoolean","COPY",EDGE,{"derivedFrom":makeQuery(id+"F3.opExtrude","SWEPT_EDGE",EDGE,{"disambiguationData":[OSD([sQuery(id+"F2.wireOp",EDGE,"E2.bottom"),sQuery(id+"F2.wireOp",EDGE,"E11"),sQuery(id+"F2.wireOp",EDGE,"E12"),sQuery(id+"F2.wireOp",EDGE,"E13")])]})});
            var Q15;
            Q15=makeQuery(id+"F3.boolean.opBoolean","COPY",EDGE,{"derivedFrom":makeQuery(id+"F3.opExtrude","SWEPT_EDGE",EDGE,{"disambiguationData":[OSD([sQuery(id+"F2.wireOp",EDGE,"E2.bottom"),sQuery(id+"F2.wireOp",EDGE,"E19.MirrorCS")])]})});
            fillet(context, id + "F8", {"entities" : qUnion([Q0, Q1, Q2, Q3, Q4, Q5, Q6, Q7, Q8, Q9, Q10, Q11, Q12, Q13, Q14, Q15]), "radius" : 5 * mm, "tangentPropagation" : true, "allowEdgeOverflow" : false});
        }
        {
            var Q0;
            Q0=makeQuery(id+"F5.opExtrude","CAP_EDGE",EDGE,{"disambiguationData":[OSD([sQuery(id+"F4.wireOp",EDGE,"E29.MirrorCS")])],"isStart":false});
            var Q1;
            Q1=makeQuery(id+"F5.opExtrude","CAP_EDGE",EDGE,{"disambiguationData":[OSD([sQuery(id+"F4.wireOp",EDGE,"E30.MirrorCS")])],"isStart":false});
            var Q2;
            Q2=makeQuery(id+"F5.opExtrude","CAP_EDGE",EDGE,{"disambiguationData":[OSD([sQuery(id+"F4.wireOp",EDGE,"E28.right")])],"isStart":false});
            var Q3;
            Q3=makeQuery(id+"F5.opExtrude","CAP_EDGE",EDGE,{"disambiguationData":[OSD([sQuery(id+"F4.wireOp",EDGE,"E28.left")])],"isStart":false});
            var Q4;
            Q4=makeQuery(id+"F5.opExtrude","CAP_EDGE",EDGE,{"disambiguationData":[OSD([sQuery(id+"F4.wireOp",EDGE,"E29.MirrorCS")])],"isStart":true});
            var Q5;
            Q5=makeQuery(id+"F5.opExtrude","CAP_EDGE",EDGE,{"disambiguationData":[OSD([sQuery(id+"F4.wireOp",EDGE,"E28.left")])],"isStart":true});
            var Q6;
            Q6=makeQuery(id+"F5.opExtrude","CAP_EDGE",EDGE,{"disambiguationData":[OSD([sQuery(id+"F4.wireOp",EDGE,"E30.MirrorCS")])],"isStart":true});
            var Q7;
            Q7=makeQuery(id+"F5.opExtrude","CAP_EDGE",EDGE,{"disambiguationData":[OSD([sQuery(id+"F4.wireOp",EDGE,"E28.right")])],"isStart":true});
            fillet(context, id + "F9", {"entities" : qUnion([Q0, Q1, Q2, Q3, Q4, Q5, Q6, Q7]), "radius" : 3.75 * mm, "tangentPropagation" : true, "allowEdgeOverflow" : false});
        }
    });
